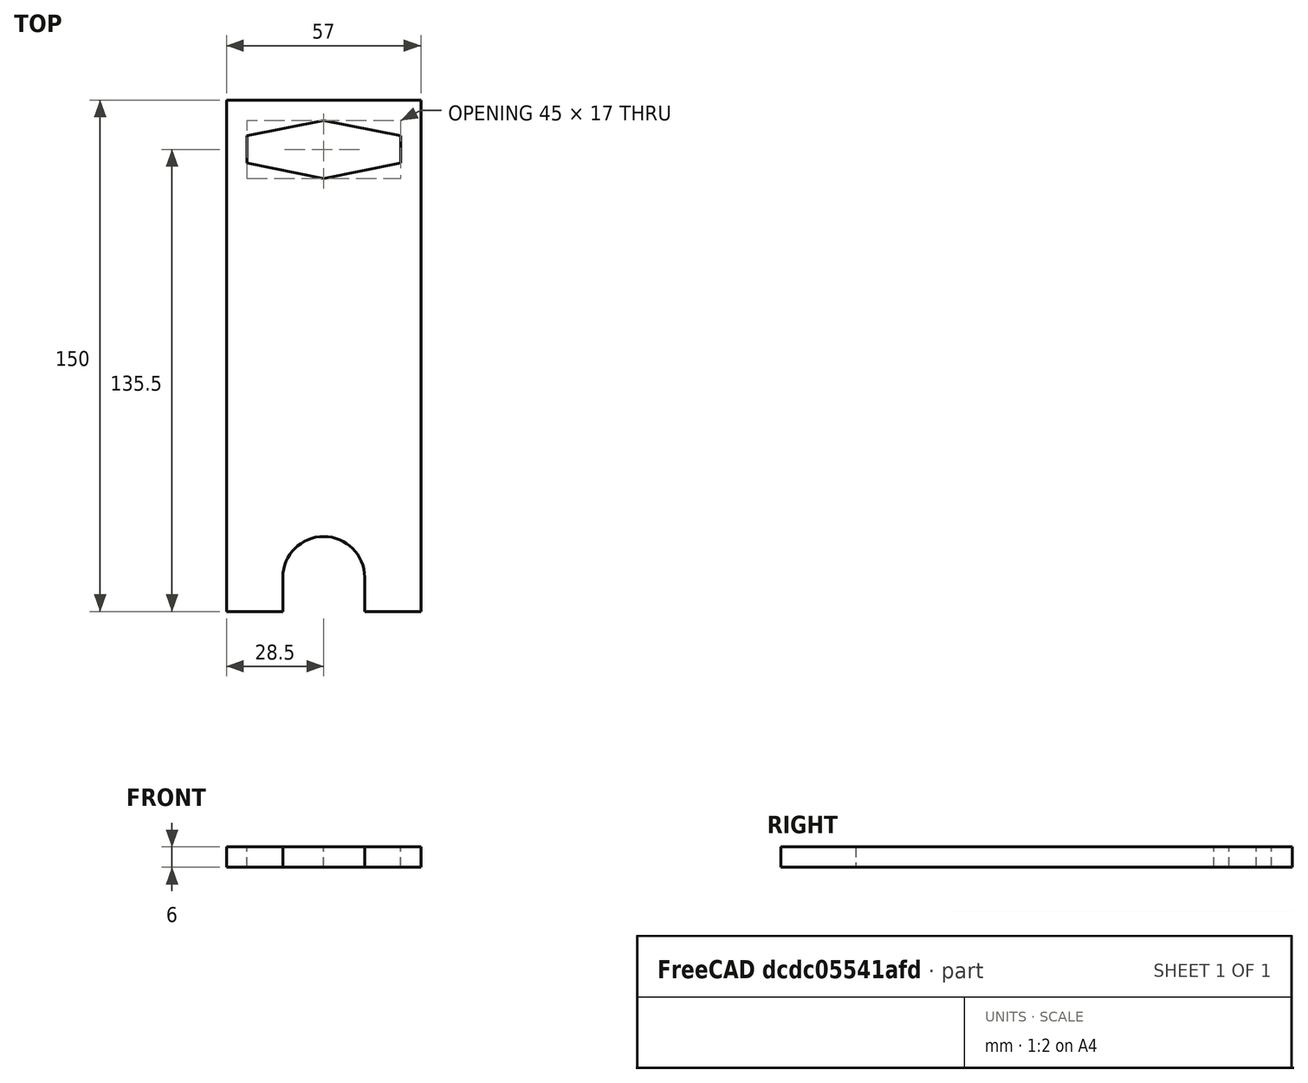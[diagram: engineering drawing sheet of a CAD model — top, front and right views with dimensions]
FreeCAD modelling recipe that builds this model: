
FCSTD DOCUMENT  (FreeCAD 2022.111R30764 (Git))
Label: door lock block
License: All rights reserved
LicenseURL: http://en.wikipedia.org/wiki/All_rights_reserved
objects: Sketcher::SketchObject×1, PartDesign::Pad×1, PartDesign::Body×1
note: 5 computed .brp shape members not serialized (recipe doc carries the construction recipe); baked Part::Feature solids carry a one-line shape summary decoded from their .brp

FEATURE [Sketcher::SketchObject] Sketch
  FullyConstrained = true
  MapMode = 5
  Support = -> [XY_Plane]
  TreeRank = 11
  sketch-geometry (15):
    g0: LineSegment StartX=0 StartY=8.5 StartZ=0 EndX=-22.5 EndY=4 EndZ=0
    g1: LineSegment StartX=-22.5 StartY=4 StartZ=0 EndX=-22.5 EndY=-4 EndZ=0
    g2: LineSegment StartX=-22.5 StartY=-4 StartZ=0 EndX=0 EndY=-8.5 EndZ=0
    g3: LineSegment StartX=0 StartY=-8.5 StartZ=0 EndX=22.5 EndY=-4 EndZ=0
    g4: LineSegment StartX=22.5 StartY=-4 StartZ=0 EndX=22.5 EndY=4 EndZ=0
    g5: LineSegment StartX=22.5 StartY=4 StartZ=0 EndX=0 EndY=8.5 EndZ=0
    g6: ArcOfCircle CenterX=0 CenterY=-125.5 CenterZ=0 NormalX=0 NormalY=0 NormalZ=1 AngleXU=0 Radius=12 StartAngle=1e-16 EndAngle=3.14159
    g7: LineSegment StartX=-12 StartY=-125.5 StartZ=0 EndX=-12 EndY=-135.5 EndZ=0
    g8: LineSegment StartX=-12 StartY=-135.5 StartZ=0 EndX=-28.5 EndY=-135.5 EndZ=0
    g9: LineSegment StartX=-28.5 StartY=-135.5 StartZ=0 EndX=-28.5 EndY=14.5 EndZ=0
    g10: LineSegment StartX=-28.5 StartY=14.5 StartZ=0 EndX=28.5 EndY=14.5 EndZ=0
    g11: LineSegment StartX=28.5 StartY=14.5 StartZ=0 EndX=28.5 EndY=-135.5 EndZ=0
    g12: LineSegment StartX=28.5 StartY=-135.5 StartZ=0 EndX=12 EndY=-135.5 EndZ=0
    g13: LineSegment StartX=12 StartY=-135.5 StartZ=0 EndX=12 EndY=-125.5 EndZ=0
    g14: GeomPoint [constr] X=0 Y=-113.5 Z=0
  constraints (38):
    c: PointOnObject(g0,g-2)
    c: Coincident(g0,g1)
    c: Coincident(g1,g2)
    c: Coincident(g2,g3)
    c: Coincident(g3,g4)
    c: Coincident(g4,g5)
    c: Coincident(g5,g0)
    c: DistanceX(g0,g4) = 45
    c: DistanceY(g2,g0) = 17
    c: Symmetric(g0,g4,g-2)
    c: DistanceY(g1,g1) = 8
    c: Symmetric(g0,g1,g-1)
    c: Symmetric(g0,g2,g-1)
    c: Symmetric(g4,g3,g-1)
    c: PointOnObject(g6,g-2)
    c: Tangent(g6,g7) = -1.5708
    c: Coincident(g7,g8)
    c: Horizontal(g8)
    c: Coincident(g8,g9)
    c: Vertical(g9)
    c: Coincident(g9,g10)
    c: Coincident(g10,g11)
    c: Vertical(g11)
    c: Coincident(g11,g12)
    c: Horizontal(g12)
    c: Coincident(g12,g13)
    c: Vertical(g13)
    c: Diameter(g6) = 24
    c: Symmetric(g9,g10,g-2)
    c: DistanceY(g0,g9) = 6
    c: DistanceX(g9,g0) = 6
    c: Horizontal(g7,g12)
    c: Tangent(g13,g6) = -1.5708
    c: DistanceY(g7,g7) = 10
    c: Vertical(g7)
    c: PointOnObject(g14,g-2)
    c: PointOnObject(g14,g6)
    c: DistanceY(g14,g2) = 105
FEATURE [PartDesign::Pad] Pad
  AddSubType = 0
  AlongSketchNormal = false
  CheckUpToFaceLimits = true
  ClaimChildren = false
  Direction = (0,0,1)
  Fit = 0
  FitJoin = 0
  InnerFit = 0
  InnerFitJoin = 0
  InnerTaperAngle = 0
  InnerTaperAngleRev = 0
  Length = 6
  Length2 = 100
  Linearize = true
  NewSolid = false
  Profile = -> Sketch
  Suppress = false
  TreeRank = 12
  Type = 0
  _ProfileBasedVersion = 1
FEATURE [PartDesign::Body] Body
  AutoGroupSolids = false
  ExportMode = 0
  Group = -> [Sketch,Pad]
  Origin = -> Origin
  Tip = -> Pad
  TreeRank = 10
  _ExportChildren = -> [Pad]
  _GroupVersion = 1
